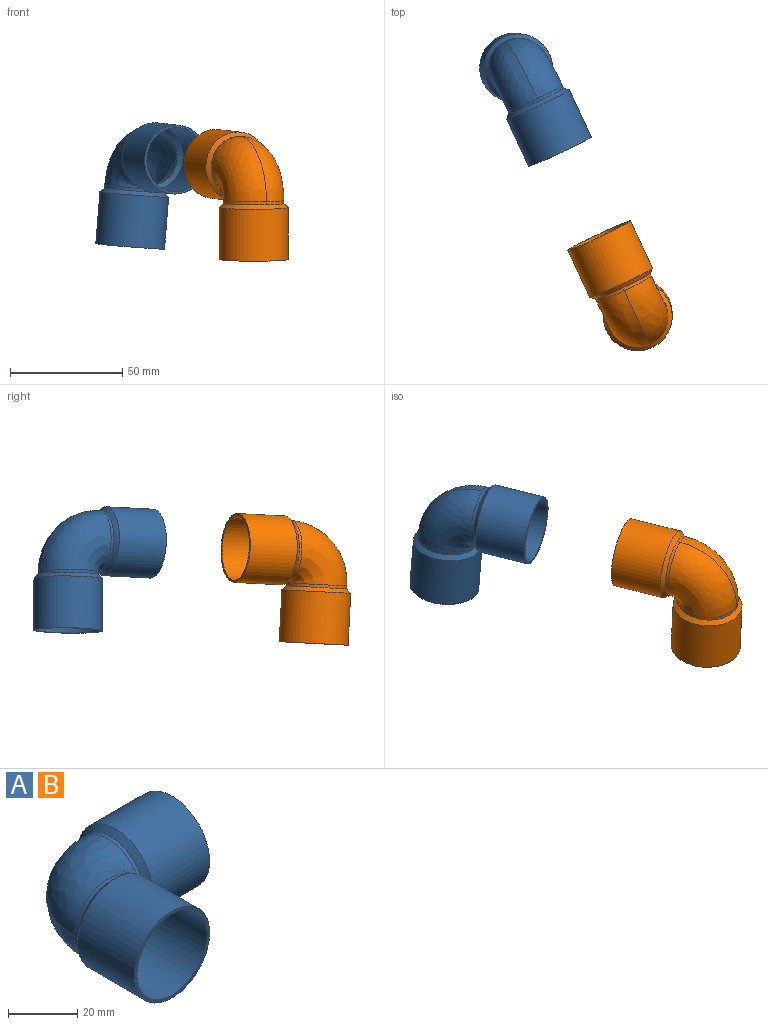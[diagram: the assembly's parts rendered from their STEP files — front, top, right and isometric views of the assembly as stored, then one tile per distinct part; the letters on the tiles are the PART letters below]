
ASSEMBLY  parts=2 mates=1
PART A: 23 faces, bbox 56x56x30.7 mm
  f0: cone r=15.34mm half-angle=45deg, axis (1,0,0), area 240.6mm2, adj f1,f2,f18
  f1: bspline ~27.11x14.37mm, area 54.8mm2, adj f0,f2,f3
  f2: bspline ~27.11x14.37mm, area 54.8mm2, adj f0,f1,f4
  f3: bspline ~30.03x30.03mm, area 953.3mm2, adj f1,f4,f5
  f4: bspline ~30.03x30.03mm, area 953.3mm2, adj f2,f3,f6
  f5: bspline ~27.11x14.37mm, area 54.8mm2, adj f3,f6,f7
  f6: bspline ~27.11x14.37mm, area 54.8mm2, adj f4,f5,f7
  f7: cone r=15.34mm half-angle=45deg, axis (0,-1,0), area 240.6mm2, adj f5,f6,f9
  f8: plane 30.68x30.68mm, normal (0,-1,0), area 94.7mm2, adj f9,f10
  f9: cylinder r=15.34mm len=30.68mm, axis (0,1,0), area 2228.1mm2, adj f7,f8
  f10: cylinder r=14.33mm len=28.65mm, axis (0,1,0), area 2080.5mm2, adj f8,f17
  f11: bspline ~25.08x13.55mm, area 25.3mm2, adj f12,f13,f20
  f12: bspline ~25.08x13.55mm, area 25.3mm2, adj f11,f14,f20
  f13: bspline ~28.49x28.49mm, area 881.3mm2, adj f11,f14,f15
  f14: bspline ~28.49x28.49mm, area 881.3mm2, adj f12,f13,f16
  f15: bspline ~25.08x13.55mm, area 50.6mm2, adj f13,f16,f17
  f16: bspline ~25.08x13.55mm, area 50.6mm2, adj f14,f15,f17
  f17: cone r=14.33mm half-angle=45deg, axis (0,-1,0), area 223.6mm2, adj f10,f15,f16
  f18: cylinder r=15.34mm len=30.68mm, axis (-1,0,0), area 2228.1mm2, adj f0,f19
  f19: plane 30.68x30.68mm, normal (1,0,0), area 94.7mm2, adj f18,f21
  f20: cone r=12.45mm half-angle=0.5deg, axis (1,0,0), area 50.7mm2, adj f11,f12,f22
  f21: cylinder r=14.33mm len=28.65mm, axis (1,0,0), area 2080.5mm2, adj f19,f22
  f22: cone r=14.33mm half-angle=44.9deg, axis (1,0,0), area 223.3mm2, adj f20,f21
PART B: same geometry as A
PLACE A rot(axis=(-0.19,0.96,0.22),96.9deg) t=(172.76,110.23,71.1)mm
PLACE B rot(axis=(0.42,0.63,0.66),136.6deg) t=(217.15,16.05,48.71)mm
MATE cylindrical A.f7 <-> B.f0  axis (-0.42,0.91,0.05) through (177.64,99.77,70.56)mm
